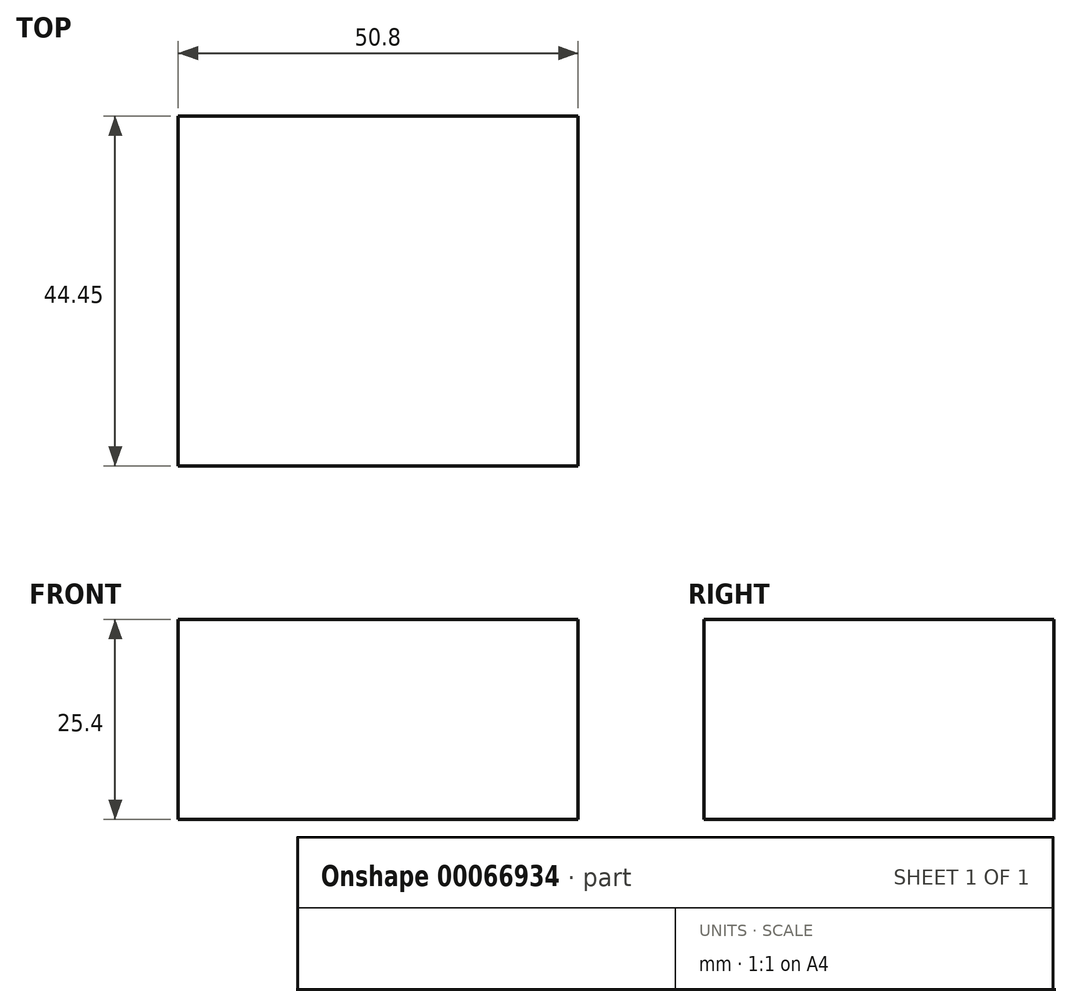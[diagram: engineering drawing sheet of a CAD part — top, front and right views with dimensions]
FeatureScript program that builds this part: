
annotation { "Feature Type Name" : "Feature", "Feature Type Description" : "" }
export const myFeature = defineFeature(function(context is Context, id is Id, definition is map)
    precondition{}
    {
        {
            var Q0;
            Q0=qCreatedBy(makeId("Top.planeOp"),FACE);
            var sketch = newSketch(context, id + "F0", { "sketchPlane" : qUnion([Q0])});
            skLineSegment(sketch, "E0.bottom", {"start": v(0, 0) * mm, "end": v(50.8, 0) * mm});
            skLineSegment(sketch, "E0.top", {"start": v(0, -44.45) * mm, "end": v(50.8, -44.45) * mm});
            skLineSegment(sketch, "E0.left", {"start": v(0, 0) * mm, "end": v(0, -44.45) * mm});
            skLineSegment(sketch, "E0.right", {"start": v(50.8, 0) * mm, "end": v(50.8, -44.45) * mm});
            skSolve(sketch);
        }
        {
            var Q0;
            Q0 = qSketchRegion(id + "F0", true);
            extrude(context, id + "F1", {"entities" : qUnion([Q0]), "depth" : 25.4 * mm});
        }
    });
